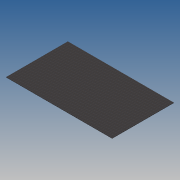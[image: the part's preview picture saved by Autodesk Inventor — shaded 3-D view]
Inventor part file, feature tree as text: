
AUTODESK INVENTOR PART (.ipt)
format: ipt  version: 2013 (Build 170138000, 138)  size: 148,992 bytes
history: native  units: in
note: dims shown in document units (in); Inventor stores cm internally (conversion verified against a paired STEP export)
features: sketch x3, extrude x2, hole x1
ambient origin geometry x8: Origin, YZ Plane, XZ Plane, XY Plane, X Axis, Y Axis, Z Axis, Center Point
bodies: Solid1 (feature_tree)
feature tree (6):
  extrude  "Extrusion1"  Depth=191.0in
  hole  "Hole1"  [1 undecoded]
  extrude  "Extrusion2"  Depth=1.75in
  sketch  "Sketch1"  dims[d0=328.0in d1=191.0in]
  sketch  "Sketch2"  dims[d2=1.0in d3=0.0in d4=1.0in]
  sketch  "Sketch3"  dims[d5=1.75in d6=1.75in d7=1.0in d8=127.25in d9=1.0in d10=103.0in d11=1.0in d12=103.25in d13=0.7874in d15=144.75in d16=0.3937in d18=1.0in d20=1.0in d21=0.75in d22=0.375in d23=0.25in d24=0.5635in d25=1.0in d26=0.8108in d27=1.0in d29=43.0in d30=0.0in]
note: 1 required parameter value undecoded (feature->parameter linkage not recoverable at this tier; creation-order binding heuristic only, values carry confidence <= 0.55)
